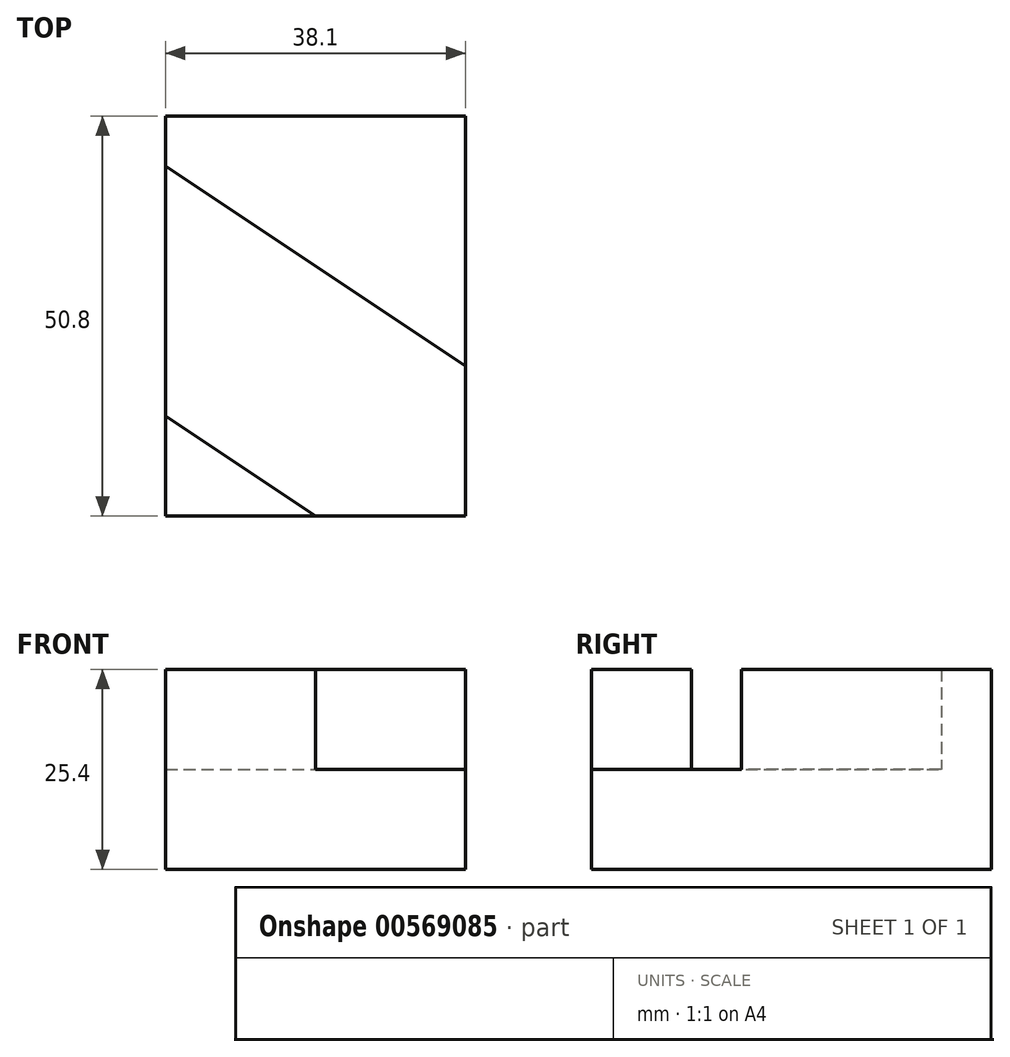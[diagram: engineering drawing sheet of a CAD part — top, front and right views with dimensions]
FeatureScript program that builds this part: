
annotation { "Feature Type Name" : "Feature", "Feature Type Description" : "" }
export const myFeature = defineFeature(function(context is Context, id is Id, definition is map)
    precondition{}
    {
        {
            var Q0;
            Q0=qCreatedBy(makeId("Top.planeOp"),FACE);
            var sketch = newSketch(context, id + "F0", { "sketchPlane" : qUnion([Q0])});
            skLineSegment(sketch, "E0", {"start": v(0, 0) * mm, "end": v(0, 50.8) * mm});
            skLineSegment(sketch, "E1", {"start": v(0, 50.8) * mm, "end": v(38.1, 50.8) * mm});
            skLineSegment(sketch, "E2", {"start": v(38.1, 50.8) * mm, "end": v(38.1, 0) * mm});
            skLineSegment(sketch, "E3", {"start": v(38.1, 0) * mm, "end": v(0, 0) * mm});
            skSolve(sketch);
        }
        {
            var Q0;
            Q0 = qSketchRegion(id + "F0", true);
            var Q1;
            Q1=makeQuery(id+"F0.imprint","IMPRINT",FACE,{"disambiguationData":[TD([[makeQuery(id+"F0.imprint","IMPRINT",EDGE,{"derivedFrom":sQuery(id+"F0.wireOp",EDGE,"E0")}),-1.0]])]});
            extrude(context, id + "F1", {"entities" : qUnion([Q0, Q1]), "depth" : 25.4 * mm, "offsetDistance" : 25.4 * mm});
        }
        {
            var Q0;
            Q0=makeQuery(id+"F1.opExtrude","CAP_FACE",FACE,{"disambiguationData":[OSD([sQuery(id+"F0.wireOp",EDGE,"E0"),sQuery(id+"F0.wireOp",EDGE,"E1"),sQuery(id+"F0.wireOp",EDGE,"E2"),sQuery(id+"F0.wireOp",EDGE,"E3")])],"isStart":false});
            var sketch = newSketch(context, id + "F2", { "sketchPlane" : qUnion([Q0])});
            skLineSegment(sketch, "E4", {"start": v(0, 44.45) * mm, "end": v(38.1, 19.05) * mm});
            skLineSegment(sketch, "E5", {"start": v(38.1, 19.05) * mm, "end": v(38.1, 50.8) * mm});
            skLineSegment(sketch, "E6", {"start": v(38.1, 50.8) * mm, "end": v(0, 50.8) * mm});
            skLineSegment(sketch, "E7", {"start": v(0, 50.8) * mm, "end": v(0, 44.45) * mm});
            skLineSegment(sketch, "E8", {"start": v(0, 0) * mm, "end": v(0, 12.7) * mm});
            skLineSegment(sketch, "E9", {"start": v(0, 12.7) * mm, "end": v(19.05, 0) * mm});
            skLineSegment(sketch, "E10", {"start": v(19.05, 0) * mm, "end": v(0, 0) * mm});
            skLineSegment(sketch, "E11", {"start": v(0, 12.7) * mm, "end": v(0, 0) * mm});
            skSolve(sketch);
        }
        {
            var Q0;
            Q0 = qSketchRegion(id + "F2", true);
            extrude(context, id + "F3", {"entities" : qUnion([Q0]), "operationType" : NewBodyOperationType.ADD, "depth" : 25.4 * mm, "offsetDistance" : 25.4 * mm});
        }
        {
            var Q0;
            Q0=makeQuery(id+"F1.opExtrude","CAP_FACE",FACE,{"disambiguationData":[OSD([sQuery(id+"F0.wireOp",EDGE,"E0"),sQuery(id+"F0.wireOp",EDGE,"E1"),sQuery(id+"F0.wireOp",EDGE,"E2"),sQuery(id+"F0.wireOp",EDGE,"E3")])],"isStart":false});
            extrude(context, id + "F4", {"entities" : qUnion([Q0]), "operationType" : NewBodyOperationType.ADD, "depth" : 12.7 * mm, "offsetDistance" : 25.4 * mm});
        }
        {
            var Q0;
            {var subQ0=sQuery(id+"F0.wireOp",EDGE,"E2");Q0=makeQuery(id+"F4.boolean.opBoolean","MERGE",FACE,{"derivedFrom":[makeQuery(id+"F3.boolean.opBoolean","MERGE",FACE,{"derivedFrom":[makeQuery(id+"F1.opExtrude","SWEPT_FACE",FACE,{"disambiguationData":[OSD([subQ0])]}),makeQuery(id+"F3.opExtrude","SWEPT_FACE",FACE,{"disambiguationData":[OSD([sQuery(id+"F2.wireOp",EDGE,"E5")])]})]}),makeQuery(id+"F4.opExtrude","SWEPT_FACE",FACE,{"disambiguationData":[OSD([subQ0])]})]});}
            var sketch = newSketch(context, id + "F5", { "sketchPlane" : qUnion([Q0])});
            skLineSegment(sketch, "E12", {"start": v(0, 25.4) * mm, "end": v(50.8, 25.4) * mm});
            skLineSegment(sketch, "E13", {"start": v(50.8, 25.4) * mm, "end": v(50.8, 0) * mm});
            skLineSegment(sketch, "E14", {"start": v(50.8, 0) * mm, "end": v(0, 0) * mm});
            skLineSegment(sketch, "E15", {"start": v(0, 0) * mm, "end": v(0, 25.4) * mm});
            skSolve(sketch);
        }
        {
            var Q0;
            Q0=makeQuery(id+"F5.imprint","IMPRINT",FACE,{"disambiguationData":[TD([[makeQuery(id+"F5.imprint","IMPRINT",EDGE,{"derivedFrom":sQuery(id+"F5.wireOp",EDGE,"E12")}),-1.0]])]});
            extrude(context, id + "F6", {"entities" : qUnion([Q0]), "operationType" : NewBodyOperationType.REMOVE, "oppositeDirection" : true, "depth" : 50.8 * mm, "offsetDistance" : 25.4 * mm});
        }
    });
